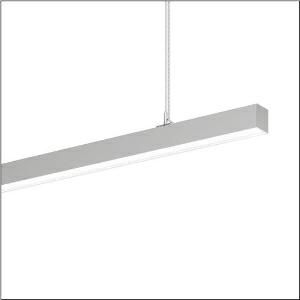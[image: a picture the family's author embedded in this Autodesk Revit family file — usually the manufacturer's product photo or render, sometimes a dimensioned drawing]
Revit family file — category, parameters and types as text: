
# Revit family: silica_r__21_51mx30da44sb_e9ec
name_source: partatom
category: Lighting Fixtures
units: mm (PartAtom-declared; Revit-internal decimal feet)

## family parameters
Cut with Voids When Loaded = No
Host = Face
Light Source = No
Part Type = Normal
Room Calculation Point = No
Round Connector Dimension = Use Diameter
Shared = No

## types (1)
- --- (1 x LED, 4210 lm, 26 W, 4000K)
    Apparent Load = 26 VA
    CIE Flux Codes = 47 79 96 57 100
    Color Rendering = 80
    Color Temperature = 4000K
    Default Elevation = 1800 mm
    Description = Silica® 21, office luminaire, primary optical cover: cover, of PMMA, opal, light emission: direct/indirect distribution, primary light characteristic: symmetric, installation type: suspended mounting, LED, rated luminous flux: 4.210lm, luminous efficacy: 162lm/W, light colour: 840, colour temperature: 4000K, with terminal, 3+2-pole, max. 2.5mm², mains connection: 220..240V, AC, 50/60Hz, rated input power: 26W, luminaire housing, of aluminium, metallic grey (RAL 9006), length: 1.204mm, width: 53mm, height: 53mm, protection rating (complete): IP20, insulation class (complete): insulation class I (protective earthing), certification: CE, permissible operating ambient temperature: 0..+35°C, standard: EN 50419, packaging unit: 1 piece
    Height = 53 mm
    Lamp = 1 x LED
    Lamp Light Flux = 4210 lm
    Lamp Power = 26 W
    Lamp count = 1
    Length = 1204 mm
    Luminous efficacy = 162 lm/W
    Manufacturer = Siteco
    ModVariant = No
    Model = 51MX30DA44SB
    Mounting Place = Ceiling
    Mounting Type = Pendant
    Number of Poles = 1
    OnlyDefault = Yes
    Power Factor = 1
    Product Name = Silica® 21
    Product group = office luminaire | ceiling pendant
    ProductGroupID = 902
    Protection Class = Protection class I
    Protection Degree = IP 20
    RLX_Detail_Level = 1
    RLX_Emergency_Light_Flux = 0 lm
    RLX_Emergency_Type = 0
    RLX_Emergency_Type_DB = No
    RlxData = <blob elided: 23201 chars, md5=7769d3dd>
    Socket = socket
    Standby Power = 0 W
    System Light Flux = 4210 lm
    System Power = 26 W
    Type Comments = factory setting: luminous flux: 100 % | dim-lin: 254 | 218 mA
    Type Image = l_1313621.jpg
    URL = http://relux.com
    VarID = @adj_065383
    Voltage = 0 V
    Weight = 0.00 kg
    Width = 53 mm

## geometry (parser evidence)
native form markers: Blend x4, Sweep x12
no freeform markers — native parametric forms only
